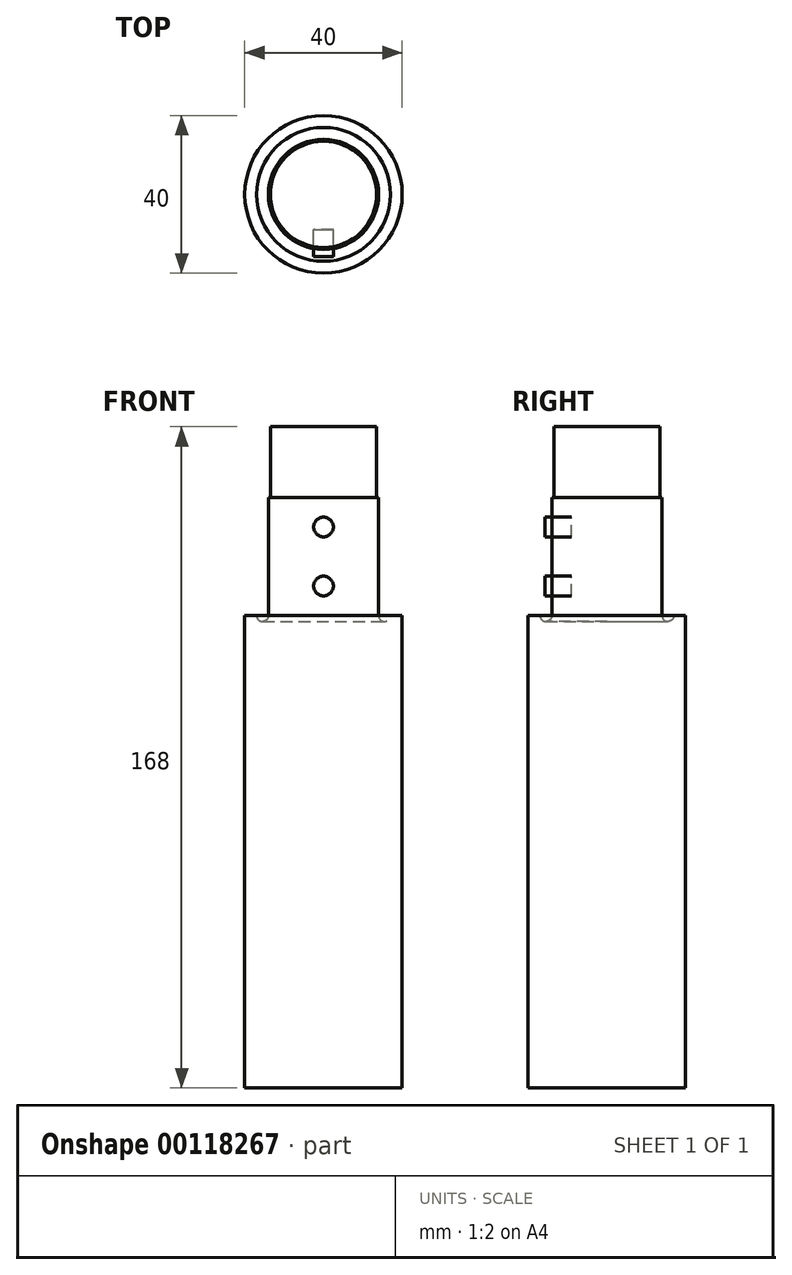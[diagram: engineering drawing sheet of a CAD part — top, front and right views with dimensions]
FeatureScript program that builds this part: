
annotation { "Feature Type Name" : "Feature", "Feature Type Description" : "" }
export const myFeature = defineFeature(function(context is Context, id is Id, definition is map)
    precondition{}
    {
        {
            var Q0;
            Q0=qCreatedBy(makeId("Front.planeOp"),FACE);
            var sketch = newSketch(context, id + "F0", { "sketchPlane" : qUnion([Q0])});
            skLineSegment(sketch, "E0", {"start": v(0, 30) * mm, "end": v(0, -120) * mm});
            skLineSegment(sketch, "E1", {"start": v(-20, -120) * mm, "end": v(-20, 0) * mm});
            skLineSegment(sketch, "E2", {"start": v(-20, 0) * mm, "end": v(-17, 0) * mm});
            skLineSegment(sketch, "E3", {"start": v(-14, 0) * mm, "end": v(-14, 30) * mm});
            skLineSegment(sketch, "E4", {"start": v(-14, 30) * mm, "end": v(0, 30) * mm});
            skLineSegment(sketch, "E5", {"start": v(-20, -120) * mm, "end": v(0, -120) * mm});
            skArc(sketch, "E6", {"start": v(-17, 0) * mm, "mid": v(-15.5, -1.5) * mm, "end": v(-14, 0) * mm});
            skLineSegment(sketch, "E7", {"start": v(0, 30) * mm, "end": v(0, 48) * mm});
            skLineSegment(sketch, "E8", {"start": v(0, 48) * mm, "end": v(-13.5, 48) * mm});
            skLineSegment(sketch, "E9", {"start": v(-13.5, 48) * mm, "end": v(-13.5, 30) * mm});
            skSolve(sketch);
        }
        {
            var Q0;
            {var subQ1=sQuery(id+"F0.wireOp",EDGE,"E0");Q0=makeQuery(id+"F0.imprint","IMPRINT",FACE,{"disambiguationData":[TD([[makeQuery(id+"F0.imprint","IMPRINT",EDGE,{"derivedFrom":subQ1}),-1.0]])]});}
            var Q1;
            {var subQ0=sQuery(id+"F0.wireOp",EDGE,"E7");Q1=makeQuery(id+"F0.imprint","IMPRINT",FACE,{"disambiguationData":[TD([[makeQuery(id+"F0.imprint","IMPRINT",EDGE,{"derivedFrom":subQ0}),1.0]])]});}
            var Q2;
            Q2=sQuery(id+"F0.wireOp",EDGE,"E0");
            revolve(context, id + "F1", {"entities" : qUnion([Q0, Q1]), "axis" : qUnion([Q2]), "revolveType" : RevolveType.FULL});
        }
        {
            var Q0;
            Q0=qCreatedBy(makeId("Front.planeOp"),FACE);
            cPlane(context, id + "F2", {"entities" : qUnion([Q0]), "cplaneType" : CPlaneType.OFFSET, "offset" : 14 * mm, "width" : 150 * mm, "height" : 150 * mm});
        }
        {
            var Q0;
            Q0=qCreatedBy(id+"F2.planeOp",FACE);
            var sketch = newSketch(context, id + "F3", { "sketchPlane" : qUnion([Q0])});
            skLineSegment(sketch, "E10.0", {"start": v(0, 30) * mm, "end": v(0, -120) * mm});
            skLineSegment(sketch, "E11.0", {"start": v(0, 30) * mm, "end": v(0, 22.5) * mm});
            skLineSegment(sketch, "E12", {"start": v(0, 0) * mm, "end": v(0, 7.5) * mm});
            skLineSegment(sketch, "E13", {"start": v(0, 7.5) * mm, "end": v(0, 10) * mm});
            skLineSegment(sketch, "E14", {"start": v(0, 22.5) * mm, "end": v(0, 30) * mm});
            skCircle(sketch, "E15", {"center": v(0, 22.5) * mm, "radius": 2.5 * mm});
            skCircle(sketch, "E16", {"center": v(0, 7.5) * mm, "radius": 2.5 * mm});
            skLineSegment(sketch, "E17", {"start": v(-2.5, 22.5) * mm, "end": v(-2.5, 7.5) * mm});
            skLineSegment(sketch, "E18", {"start": v(2.5, 7.5) * mm, "end": v(2.5, 22.5) * mm});
            skLineSegment(sketch, "E19.trimOffspring", {"start": v(0, 20) * mm, "end": v(0, 22.5) * mm});
            skLineSegment(sketch, "E20.trimOffspring", {"start": v(0, 10) * mm, "end": v(0, -120) * mm});
            skSolve(sketch);
        }
        {
            var Q0;
            {var subQ0=sQuery(id+"F3.wireOp",EDGE,"E10.0");Q0=makeQuery(id+"F3.imprint","IMPRINT",FACE,{"disambiguationData":[TD([[makeQuery(id+"F3.imprint","IMPRINT",EDGE,{"derivedFrom":subQ0}),-1.0]])]});}
            var Q1;
            {var subQ0=sQuery(id+"F3.wireOp",EDGE,"E10.0");Q1=makeQuery(id+"F3.imprint","IMPRINT",FACE,{"disambiguationData":[TD([[makeQuery(id+"F3.imprint","IMPRINT",EDGE,{"derivedFrom":subQ0}),1.0]])]});}
            var Q2;
            {var subQ0=sQuery(id+"F3.wireOp",EDGE,"E19.trimOffspring");Q2=makeQuery(id+"F3.imprint","IMPRINT",FACE,{"disambiguationData":[TD([[makeQuery(id+"F3.imprint","IMPRINT",EDGE,{"derivedFrom":subQ0}),-1.0]])]});}
            var Q3;
            {var subQ0=sQuery(id+"F3.wireOp",EDGE,"E19.trimOffspring");Q3=makeQuery(id+"F3.imprint","IMPRINT",FACE,{"disambiguationData":[TD([[makeQuery(id+"F3.imprint","IMPRINT",EDGE,{"derivedFrom":subQ0}),1.0]])]});}
            var Q4;
            {var subQ0=sQuery(id+"F3.wireOp",EDGE,"E20.trimOffspring");var subQ5=makeQuery(id+"F3.imprint","IMPRINT",VERTEX,{"derivedFrom":subQ0});Q4=makeQuery(id+"F3.imprint","IMPRINT",FACE,{"disambiguationData":[TD([[makeQuery(id+"F3.imprint","IMPRINT",EDGE,{"disambiguationData":[TD([[subQ5,-1.0]])],"derivedFrom":subQ0}),1.0]])]});}
            var Q5;
            {var subQ0=sQuery(id+"F3.wireOp",EDGE,"E20.trimOffspring");var subQ5=makeQuery(id+"F3.imprint","IMPRINT",VERTEX,{"derivedFrom":subQ0});Q5=makeQuery(id+"F3.imprint","IMPRINT",FACE,{"disambiguationData":[TD([[makeQuery(id+"F3.imprint","IMPRINT",EDGE,{"disambiguationData":[TD([[subQ5,-1.0]])],"derivedFrom":subQ0}),-1.0]])]});}
            extrude(context, id + "F4", {"entities" : qUnion([Q0, Q1, Q2, Q3, Q4, Q5]), "depth" : 1.75 * mm, "hasSecondDirection" : true, "secondDirectionOppositeDirection" : true, "secondDirectionDepth" : 5 * mm});
        }
    });
